# Revit family: 111011001209001
name_source: partatom
category: Modelos genéricos
revit_build: Autodesk Revit 2018 (Build: 20190510_1515(x64)
units: mm (PartAtom-declared; Revit-internal decimal feet)

## family parameters
Compartido = No
Corte con vacíos al cargar = No
Cota de conector redondo = Diámetro de uso
Puede alojar armadura = No
Punto de cálculo de habitación = No
Se basa en plano de trabajo = No
Siempre vertical = No
Tipo de pieza = Normal

## types (1)
- ESPACIADOR CON TOMADOR DE 2MM
    Aplicacion = Espaciador de cerámico con pestaña para retiro.
    Color = Blanco
    Descripción = Sistema con agarres para simplificar la introducción y extracción de los espaciadores.
    Dimension = 0 mm  [stored 0 ft]
    Empresa = CNP SPA.
    Espesor = 0 mm  [stored 0 ft]
    Material = PP
    Modelo = ESPACIADOR CON TOMADOR DE 2MM
    Nombre SKU = ESPACIADOR CERAMICA PP 2MM BLANCO BOLSA 200UN
    Num SKUs = 111011001209001
    URL = https://www.empresascnp.cl
    Unidad = Bolsas de 200 UN
    Url Ficha tecnica = https://empresascnp.cl
    Uso = Separadores diseñados para ayudar a instalar cerámica con separaciones uniformes. Son
usados entre cerámica y bordes para proveer la junta de lechada (fragüe) óptima. Su diseño permite
gran eficiencia en alineación de canteras.
    Ventajas = fácil de retirar.

note: [stored X ft] marks values corroborated as IEEE doubles in the binary element streams (Revit-internal decimal feet)

## geometry (parser evidence)
native form markers: Sweep x2
no freeform markers — native parametric forms only
